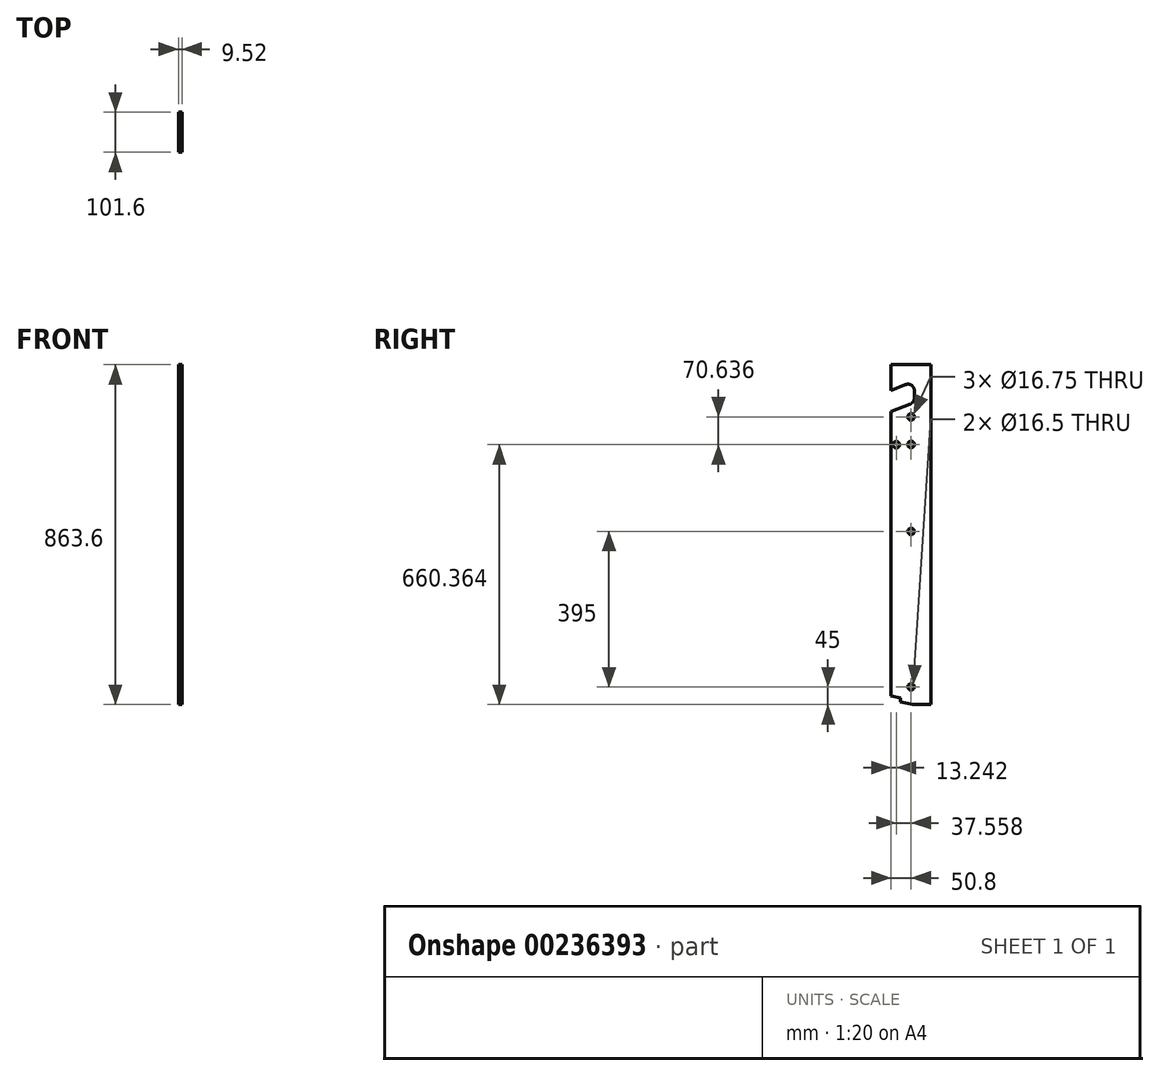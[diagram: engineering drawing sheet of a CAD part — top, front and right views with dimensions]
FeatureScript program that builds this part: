
annotation { "Feature Type Name" : "Feature", "Feature Type Description" : "" }
export const myFeature = defineFeature(function(context is Context, id is Id, definition is map)
    precondition{}
    {
        {
            var Q0;
            Q0=qCreatedBy(makeId("Right.planeOp"),FACE);
            var sketch = newSketch(context, id + "F0", { "sketchPlane" : qUnion([Q0])});
            skLineSegment(sketch, "E0.bottom", {"start": v(0, 0) * mm, "end": v(101.6, 0) * mm});
            skLineSegment(sketch, "E0.top", {"start": v(0, 863.6) * mm, "end": v(101.6, 863.6) * mm});
            skLineSegment(sketch, "E0.left", {"start": v(0, 0) * mm, "end": v(0, 863.6) * mm});
            skLineSegment(sketch, "E0.right", {"start": v(101.6, 0) * mm, "end": v(101.6, 863.6) * mm});
            skSolve(sketch);
        }
        {
            var Q0;
            Q0 = qSketchRegion(id + "F0", true);
            extrude(context, id + "F1", {"entities" : qUnion([Q0]), "endBound" : BoundingType.SYMMETRIC, "depth" : 9.52 * mm});
        }
        {
            var Q0;
            Q0=makeQuery(id+"F1.opExtrude","CAP_FACE",FACE,{"disambiguationData":[OSD([sQuery(id+"F0.wireOp",EDGE,"E0.bottom"),sQuery(id+"F0.wireOp",EDGE,"E0.top"),sQuery(id+"F0.wireOp",EDGE,"E0.left"),sQuery(id+"F0.wireOp",EDGE,"E0.right")])],"isStart":true});
            var sketch = newSketch(context, id + "F2", { "sketchPlane" : qUnion([Q0])});
            skCircle(sketch, "E1", {"center": v(-50.8, 45) * mm, "radius": 8.25 * mm});
            skCircle(sketch, "E2", {"center": v(-50.8, 440) * mm, "radius": 8.25 * mm});
            skLineSegment(sketch, "E3", {"start": v(-50.8, 0) * mm, "end": v(-50.8, 45) * mm, "construction": true});
            skLineSegment(sketch, "E4", {"start": v(-50.8, 45) * mm, "end": v(-50.8, 440) * mm, "construction": true});
            skSolve(sketch);
        }
        {
            var Q0;
            Q0 = qSketchRegion(id + "F2", true);
            extrude(context, id + "F3", {"entities" : qUnion([Q0]), "operationType" : NewBodyOperationType.REMOVE, "endBound" : BoundingType.THROUGH_ALL, "oppositeDirection" : true, "depth" : 25 * mm});
        }
        {
            var Q0;
            Q0=makeQuery(id+"F1.opExtrude","CAP_FACE",FACE,{"disambiguationData":[OSD([sQuery(id+"F0.wireOp",EDGE,"E0.bottom"),sQuery(id+"F0.wireOp",EDGE,"E0.top"),sQuery(id+"F0.wireOp",EDGE,"E0.left"),sQuery(id+"F0.wireOp",EDGE,"E0.right")])],"isStart":false});
            var sketch = newSketch(context, id + "F4", { "sketchPlane" : qUnion([Q0])});
            skLineSegment(sketch, "E5", {"start": v(0, 798) * mm, "end": v(0, 744.07) * mm});
            skLineSegment(sketch, "E6", {"start": v(0, 744.07) * mm, "end": v(59, 767.91) * mm});
            skLineSegment(sketch, "E7", {"start": v(59, 767.91) * mm, "end": v(59, 821.84) * mm});
            skLineSegment(sketch, "E8", {"start": v(59, 821.84) * mm, "end": v(0, 798) * mm});
            skLineSegment(sketch, "E9", {"start": v(50.8, 45) * mm, "end": v(-54.87, 45) * mm, "construction": true});
            skSolve(sketch);
        }
        {
            var Q0;
            Q0=makeQuery(id+"F4.imprint","IMPRINT",FACE,{"disambiguationData":[TD([[makeQuery(id+"F4.imprint","IMPRINT",EDGE,{"derivedFrom":sQuery(id+"F4.wireOp",EDGE,"E5")}),-1.0]])]});
            extrude(context, id + "F5", {"entities" : qUnion([Q0]), "operationType" : NewBodyOperationType.REMOVE, "endBound" : BoundingType.THROUGH_ALL, "oppositeDirection" : true, "depth" : 25 * mm});
        }
        {
            var Q0;
            Q0=makeQuery(id+"F5.boolean.opBoolean","COPY",EDGE,{"derivedFrom":makeQuery(id+"F5.opExtrude","SWEPT_EDGE",EDGE,{"disambiguationData":[OSD([sQuery(id+"F4.wireOp",EDGE,"E6"),sQuery(id+"F4.wireOp",EDGE,"E7")])]})});
            var Q1;
            Q1=makeQuery(id+"F5.boolean.opBoolean","COPY",EDGE,{"derivedFrom":makeQuery(id+"F5.opExtrude","SWEPT_EDGE",EDGE,{"disambiguationData":[OSD([sQuery(id+"F4.wireOp",EDGE,"E7"),sQuery(id+"F4.wireOp",EDGE,"E8")])]})});
            fillet(context, id + "F6", {"entities" : qUnion([Q0, Q1]), "radius" : 16 * mm, "tangentPropagation" : true, "allowEdgeOverflow" : false});
        }
        {
            var Q0;
            Q0=qCreatedBy(makeId("Right.planeOp"),FACE);
            var sketch = newSketch(context, id + "F7", { "sketchPlane" : qUnion([Q0])});
            skLineSegment(sketch, "E10", {"start": v(0, 0) * mm, "end": v(0, 22.54) * mm});
            skLineSegment(sketch, "E11", {"start": v(0, 22.54) * mm, "end": v(24, 17) * mm});
            skLineSegment(sketch, "E12", {"start": v(24, 17) * mm, "end": v(24, 7.25) * mm});
            skLineSegment(sketch, "E13", {"start": v(55.4, 0) * mm, "end": v(0, 0) * mm});
            skLineSegment(sketch, "E14", {"start": v(24, 7.25) * mm, "end": v(55.4, 0) * mm});
            skPoint(sketch, "E15.orphan", {"position": v(24, 0) * mm});
            skSolve(sketch);
        }
        {
            var Q0;
            Q0 = qSketchRegion(id + "F7", true);
            extrude(context, id + "F8", {"entities" : qUnion([Q0]), "operationType" : NewBodyOperationType.REMOVE, "endBound" : BoundingType.THROUGH_ALL, "oppositeDirection" : true, "depth" : 25 * mm, "hasSecondDirection" : true, "secondDirectionBound" : SecondDirectionBoundingType.THROUGH_ALL, "secondDirectionOppositeDirection" : false, "secondDirectionDepth" : 25 * mm});
        }
        {
            var Q0;
            Q0=makeQuery(id+"F1.opExtrude","CAP_FACE",FACE,{"disambiguationData":[OSD([sQuery(id+"F0.wireOp",EDGE,"E0.bottom"),sQuery(id+"F0.wireOp",EDGE,"E0.top"),sQuery(id+"F0.wireOp",EDGE,"E0.left"),sQuery(id+"F0.wireOp",EDGE,"E0.right")])],"isStart":false});
            var sketch = newSketch(context, id + "F9", { "sketchPlane" : qUnion([Q0])});
            skLineSegment(sketch, "E16", {"start": v(50.8, 440) * mm, "end": v(50.8, 661) * mm});
            skLineSegment(sketch, "E17", {"start": v(50.8, 661) * mm, "end": v(50.8, 731) * mm});
            skLineSegment(sketch, "E18", {"start": v(50.8, 731) * mm, "end": v(13.24, 660.36) * mm});
            skSolve(sketch);
        }
        {
            var Q0;
            Q0=sQuery(id+"F9.wireOp",VERTEX,"E17.end");
            var Q1;
            Q1=sQuery(id+"F9.wireOp",VERTEX,"E17.start");
            var Q2;
            Q2=sQuery(id+"F9.wireOp",VERTEX,"E18.end");
            var Q3;
            Q3=makeQuery(id+"F1.opExtrude","SWEPT_BODY",BODY,{"disambiguationData":[OSD([sQuery(id+"F0.wireOp",EDGE,"E0.bottom"),sQuery(id+"F0.wireOp",EDGE,"E0.top"),sQuery(id+"F0.wireOp",EDGE,"E0.left"),sQuery(id+"F0.wireOp",EDGE,"E0.right")])]});
            hole(context, id + "F10", {"style" : HoleStyle.SIMPLE, "endStyle" : HoleEndStyle.THROUGH, "standardTappedOrClearance" : lookupTablePath({ "standard" : "ISO", "fit" : "Close", "size" : "M16", "type" : "Clearance" }), "standardBlindInLast" : lookupTablePath({ "fit" : "Close", "standard" : "ISO", "size" : "M16", "type" : "Clearance" }), "holeDiameter" : 16.75 * mm, "tappedDepth" : 12 * mm, "tapClearance" : 3, "locations" : qUnion([Q0, Q1, Q2]), "scope" : qUnion([Q3])});
        }
    });
